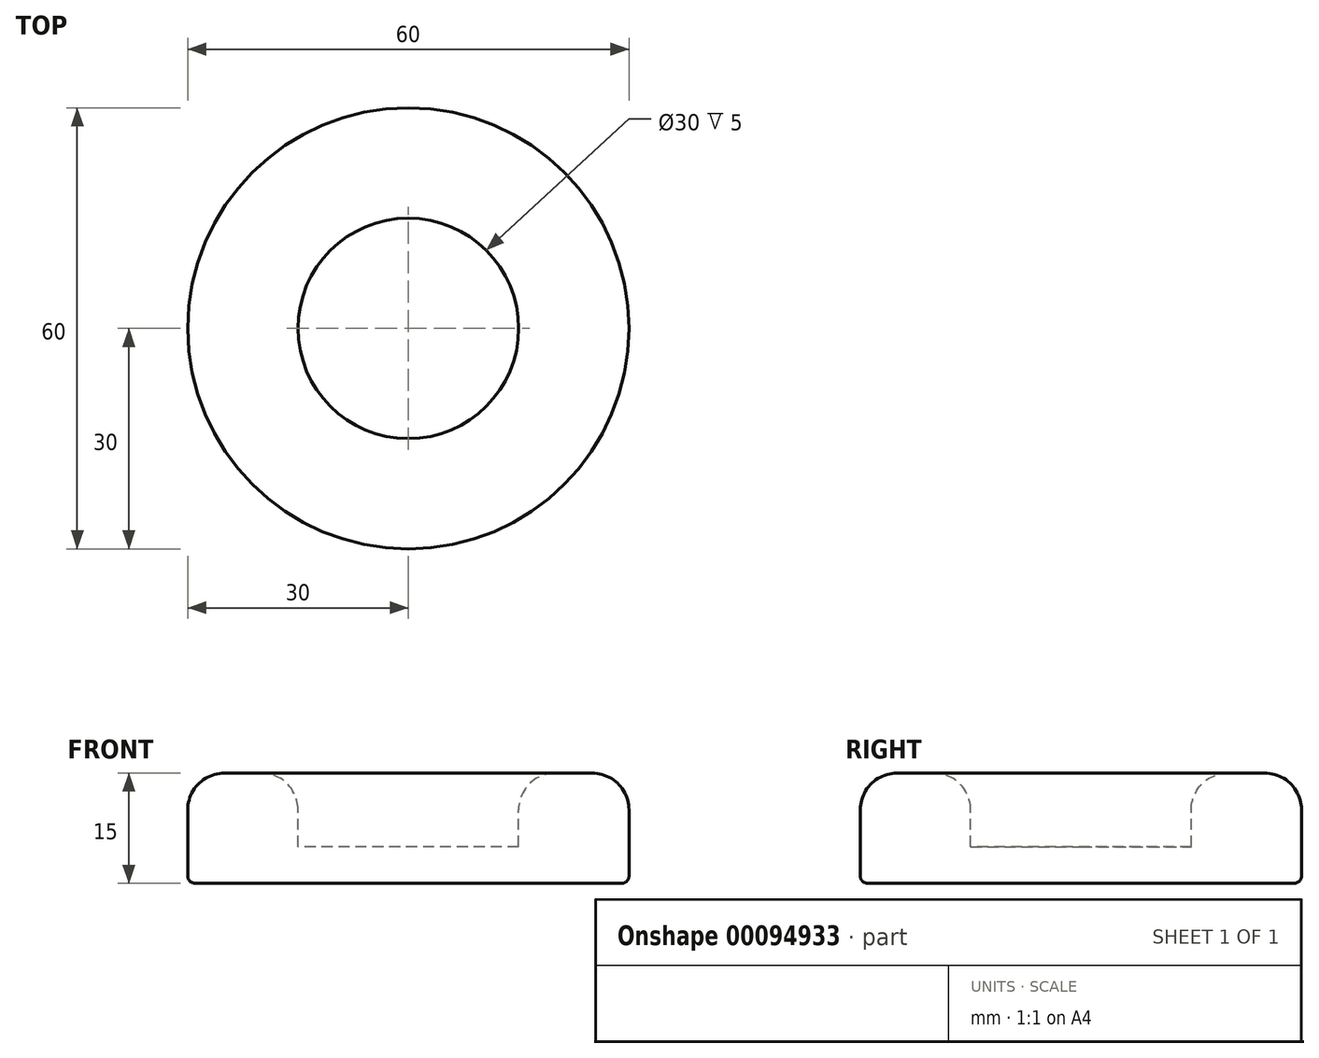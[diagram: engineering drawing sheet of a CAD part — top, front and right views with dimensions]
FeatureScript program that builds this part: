
annotation { "Feature Type Name" : "Feature", "Feature Type Description" : "" }
export const myFeature = defineFeature(function(context is Context, id is Id, definition is map)
    precondition{}
    {
        {
            var Q0;
            Q0=qCreatedBy(makeId("Front.planeOp"),FACE);
            var sketch = newSketch(context, id + "F0", { "sketchPlane" : qUnion([Q0])});
            skLineSegment(sketch, "E0", {"start": v(0, 0) * mm, "end": v(30, 0) * mm});
            skLineSegment(sketch, "E1", {"start": v(30, 0) * mm, "end": v(30, 10) * mm});
            skLineSegment(sketch, "E2", {"start": v(25, 15) * mm, "end": v(20, 15) * mm});
            skLineSegment(sketch, "E3", {"start": v(15, 10) * mm, "end": v(15, 5) * mm});
            skLineSegment(sketch, "E4", {"start": v(15, 5) * mm, "end": v(0, 5) * mm});
            skLineSegment(sketch, "E5", {"start": v(0, 5) * mm, "end": v(0, 0) * mm});
            skPoint(sketch, "E6.visualSharp", {"position": v(30, 15) * mm});
            skArc(sketch, "E6.filletArc", {"start": v(30, 10) * mm, "mid": v(28.54, 13.54) * mm, "end": v(25, 15) * mm});
            skPoint(sketch, "E7.visualSharp", {"position": v(15, 15) * mm});
            skArc(sketch, "E7.filletArc", {"start": v(20, 15) * mm, "mid": v(16.46, 13.54) * mm, "end": v(15, 10) * mm});
            skSolve(sketch);
        }
        {
            var Q0;
            Q0 = qSketchRegion(id + "F0", true);
            var Q1;
            Q1=sQuery(id+"F0.wireOp",EDGE,"E5");
            revolve(context, id + "F1", {"entities" : qUnion([Q0]), "axis" : qUnion([Q1]), "revolveType" : RevolveType.FULL});
        }
        {
            var Q0;
            Q0=makeQuery(id+"F1.opRevolve","SWEPT_FACE",FACE,{"disambiguationData":[OSD([sQuery(id+"F0.wireOp",EDGE,"E0")])]});
            fillet(context, id + "F2", {"entities" : qUnion([Q0]), "radius" : 1 * mm, "tangentPropagation" : true, "allowEdgeOverflow" : false});
        }
    });
